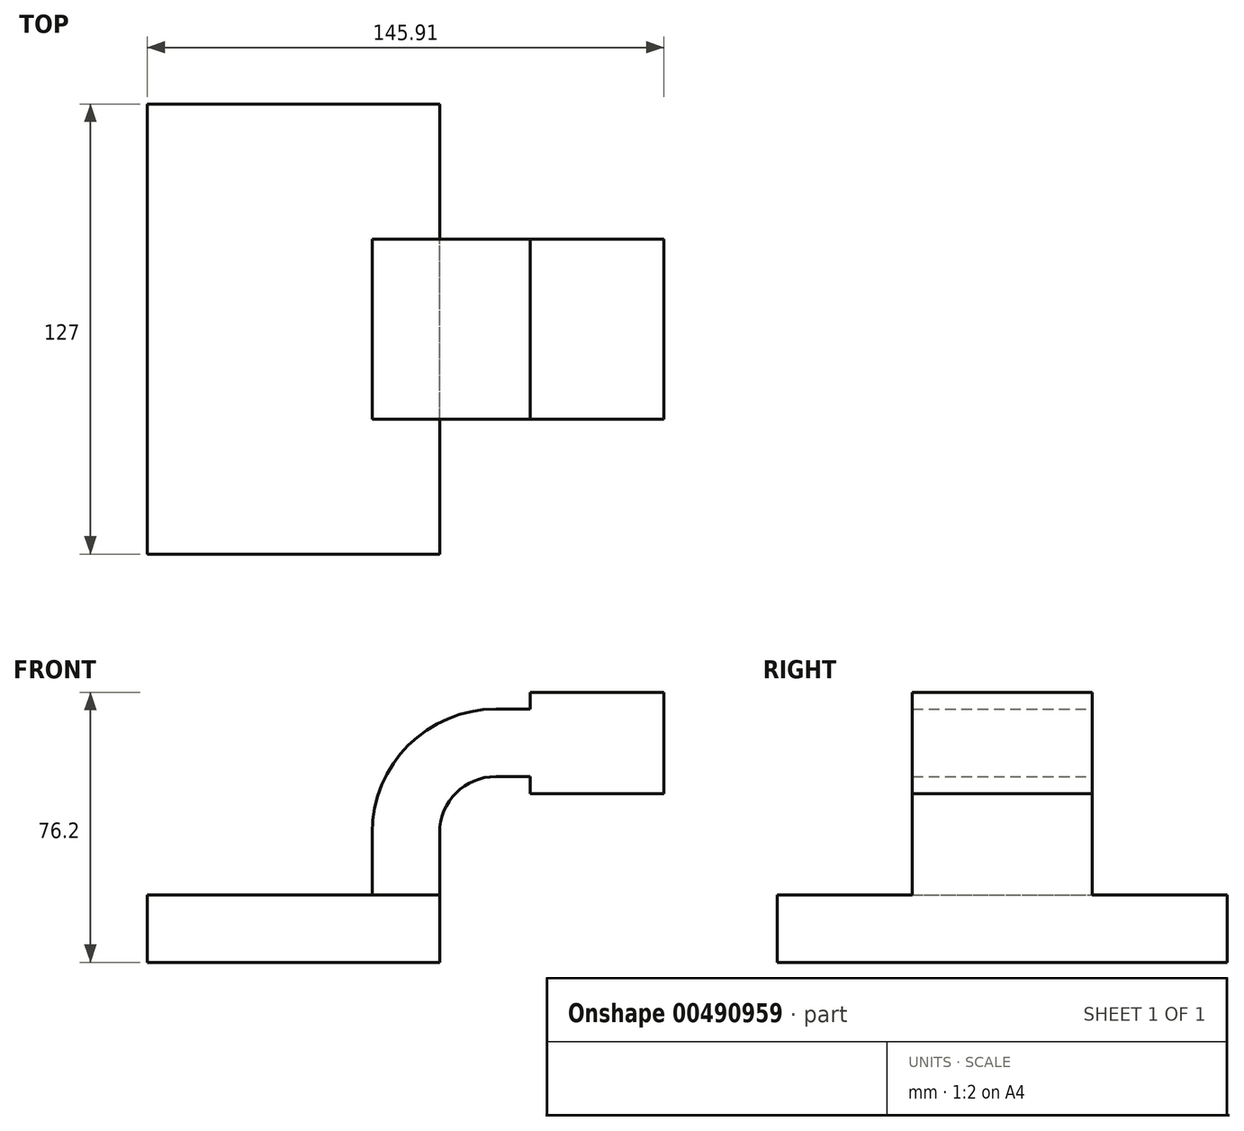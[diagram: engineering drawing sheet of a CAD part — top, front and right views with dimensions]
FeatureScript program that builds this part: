
annotation { "Feature Type Name" : "Feature", "Feature Type Description" : "" }
export const myFeature = defineFeature(function(context is Context, id is Id, definition is map)
    precondition{}
    {
        {
            var Q0;
            Q0=qCreatedBy(makeId("Front.planeOp"),FACE);
            var sketch = newSketch(context, id + "F0", { "sketchPlane" : qUnion([Q0])});
            skLineSegment(sketch, "E0.bottom", {"start": v(41.27, 9.53) * mm, "end": v(-41.28, 9.53) * mm});
            skLineSegment(sketch, "E0.top", {"start": v(41.28, -9.52) * mm, "end": v(-41.27, -9.52) * mm});
            skLineSegment(sketch, "E0.left", {"start": v(41.28, 9.53) * mm, "end": v(41.28, -9.52) * mm});
            skLineSegment(sketch, "E0.right", {"start": v(-41.28, 9.53) * mm, "end": v(-41.27, -9.52) * mm});
            skPoint(sketch, "E0.middle", {"position": v(0, 0) * mm});
            skLineSegment(sketch, "E1.bottom", {"start": v(66.82, 66.68) * mm, "end": v(104.63, 66.68) * mm});
            skLineSegment(sketch, "E1.top", {"start": v(66.82, 38.1) * mm, "end": v(104.63, 38.1) * mm});
            skLineSegment(sketch, "E1.left", {"start": v(66.82, 66.68) * mm, "end": v(66.82, 38.1) * mm});
            skLineSegment(sketch, "E1.right", {"start": v(104.63, 66.68) * mm, "end": v(104.63, 38.1) * mm});
            skPoint(sketch, "E1.middle", {"position": v(85.73, 52.39) * mm});
            skLineSegment(sketch, "E2", {"start": v(41.27, 9.53) * mm, "end": v(41.27, 27) * mm});
            skArc(sketch, "E3", {"start": v(41.27, 27) * mm, "mid": v(45.92, 38.23) * mm, "end": v(57.15, 42.88) * mm});
            skLineSegment(sketch, "E4", {"start": v(57.15, 42.88) * mm, "end": v(85.73, 42.88) * mm});
            skLineSegment(sketch, "E5.0", {"start": v(57.15, 61.93) * mm, "end": v(85.73, 61.93) * mm});
            skArc(sketch, "E5.1", {"start": v(22.23, 27) * mm, "mid": v(32.45, 51.7) * mm, "end": v(57.15, 61.93) * mm});
            skLineSegment(sketch, "E5.2", {"start": v(22.22, 9.53) * mm, "end": v(22.22, 27) * mm});
            skLineSegment(sketch, "E6", {"start": v(85.73, 38.1) * mm, "end": v(85.73, 66.68) * mm});
            skFitSpline(sketch, "E7", {"points": [v(-41.28, 9.53) * mm, v(57.15, 61.93) * mm], "startDerivative": vector(-8.95, 92.06) * mm, "endDerivative": vector(114.34, -16.95) * mm});
            skPoint(sketch, "E8.1.internal.snap0", {"position": v(32.45, 51.7) * mm});
            skSolve(sketch);
        }
        {
            var Q0;
            Q0=makeQuery(id+"F0.imprint","IMPRINT",FACE,{"disambiguationData":[TD([[makeQuery(id+"F0.imprint","IMPRINT",EDGE,{"derivedFrom":sQuery(id+"F0.wireOp",EDGE,"E0.top")}),-1.0]])]});
            extrude(context, id + "F1", {"entities" : qUnion([Q0]), "endBound" : BoundingType.SYMMETRIC, "depth" : 127 * mm});
        }
        {
            var Q0;
            {var subQ1=sQuery(id+"F0.wireOp",EDGE,"E2");Q0=makeQuery(id+"F0.imprint","IMPRINT",FACE,{"disambiguationData":[TD([[makeQuery(id+"F0.imprint","IMPRINT",EDGE,{"derivedFrom":subQ1}),1.0]])]});}
            var Q1;
            {var subQ0=sQuery(id+"F0.wireOp",EDGE,"E5.0");var subQ1=sQuery(id+"F0.wireOp",EDGE,"E1.left");var subQ2=makeQuery(id+"F0.imprint","INTERSECT",VERTEX,{"derivedFrom":[subQ1,subQ0]});Q1=makeQuery(id+"F0.imprint","IMPRINT",FACE,{"disambiguationData":[TD([[makeQuery(id+"F0.imprint","IMPRINT",EDGE,{"disambiguationData":[TD([[subQ2,-1.0]])],"derivedFrom":subQ1}),1.0]])]});}
            var Q2;
            {var subQ0=sQuery(id+"F0.wireOp",EDGE,"E1.right");Q2=makeQuery(id+"F0.imprint","IMPRINT",FACE,{"disambiguationData":[TD([[makeQuery(id+"F0.imprint","IMPRINT",EDGE,{"derivedFrom":subQ0}),-1.0]])]});}
            var Q3;
            {var subQ0=sQuery(id+"F0.wireOp",EDGE,"E1.left");var subQ1=sQuery(id+"F0.wireOp",EDGE,"E1.bottom");var subQ2=makeQuery(id+"F0.imprint","INTERSECT",VERTEX,{"derivedFrom":[subQ1,subQ0]});Q3=makeQuery(id+"F0.imprint","IMPRINT",FACE,{"disambiguationData":[TD([[makeQuery(id+"F0.imprint","IMPRINT",EDGE,{"disambiguationData":[TD([[subQ2,-1.0]])],"derivedFrom":subQ1}),-1.0]])]});}
            var Q4;
            {var subQ0=sQuery(id+"F0.wireOp",EDGE,"E1.left");var subQ1=sQuery(id+"F0.wireOp",EDGE,"E1.top");var subQ2=makeQuery(id+"F0.imprint","INTERSECT",VERTEX,{"derivedFrom":[subQ1,subQ0]});Q4=makeQuery(id+"F0.imprint","IMPRINT",FACE,{"disambiguationData":[TD([[makeQuery(id+"F0.imprint","IMPRINT",EDGE,{"disambiguationData":[TD([[subQ2,-1.0]])],"derivedFrom":subQ1}),1.0]])]});}
            extrude(context, id + "F2", {"entities" : qUnion([Q0, Q1, Q2, Q3, Q4]), "operationType" : NewBodyOperationType.ADD, "endBound" : BoundingType.SYMMETRIC, "depth" : 50.8 * mm});
        }
        {
            var Q0;
            Q0=makeQuery(id+"F0.imprint","IMPRINT",FACE,{"disambiguationData":[TD([[makeQuery(id+"F0.imprint","IMPRINT",EDGE,{"derivedFrom":sQuery(id+"F0.wireOp",EDGE,"E5.1")}),1.0]])]});
            extrude(context, id + "F3", {"entities" : qUnion([Q0]), "operationType" : NewBodyOperationType.ADD, "endBound" : BoundingType.SYMMETRIC, "depth" : 15.88 * mm});
        }
    });
